# Revit family: Domotics-DomesticRanges-GEWISS-CHORUS_SIGNALLING-LAMP_ANTIBLACKOUT_1M
name_source: partatom
category: Apparecchi elettrici
revit_build: Autodesk Revit 2016 (Build: 20161004_0715(x64)
units: mm (PartAtom-declared; Revit-internal decimal feet)

## family parameters
Condiviso = Sì
Host = Superficie
Mantenere orientamento annotazione = Sì
Punto di calcolo locali = Sì
Quota connettore circolare = Usa diametro
Taglio con vuoti quando caricato = Sì
Tipo di parte = Normale

## types (3) — shared parameters
Altezza_copriforo = 45 mm  [stored 0.147638 ft]
Catalogue = DOMOTICS
Catalogue Range = CHORUS - DOMESTIC RANGE
Description. = Anti black-out lamp
Duration = 1H
Electrocod = 0781
IDF = 2ababe84-dc9d-4690-be76-d0d2c53a9b4a
IDT = d58e55f1-d7ef-43b1-a699-4f7e8fb50383
Immagine tipo = GW14662.jpg
Lamp = LED
Larghezza copriforo = 23 mm  [stored 0.0754593 ft]
Minimum autonomy = 1H
No. Chorus modules = 1
No. Chorus modules: = 1
Power supply batteries = Ni - Mh
Produttore = GEWISS S.p.A.
Prospetto di default = 1219 mm
SEO = Lamp
Supply voltage = 230 V ac - 50/60 Hz
Technical sheet = https://www.gewiss.com
Tipo_ = CHORUS LAMPADE ANTIBLACK-OUT 1M : GW14662 Lampada anti black-out 1M titanio
Type of lamp = LED
URL = https://www.gewiss.com
Version file RFA = 19.0
finitura = GEWISS TITANIO

## per-type parameters (varying)
| type | Colour | Descrizione | EAN code | Modello |
| GW12662 - Anti black-out lamp.1m black | Black | ANTI BLACK-OUT LAMP.1M BLACK | 8011564294998 | GW12662 |
| GW10662 - Anti black-out lamp.1m white | White | ANTI BLACK-OUT LAMP.1M WHITE | 8011564294967 | GW10662 |
| GW14662 - Anti black-out lamp.1m titanium | Titanium | ANTI BLACK-OUT LAMP.1M TITANIUM | 8011564295049 | GW14662 |

note: [stored X ft] marks values corroborated as IEEE doubles in the binary element streams (Revit-internal decimal feet)

## geometry (parser evidence)
native form markers: Sweep x4
no freeform markers — native parametric forms only
